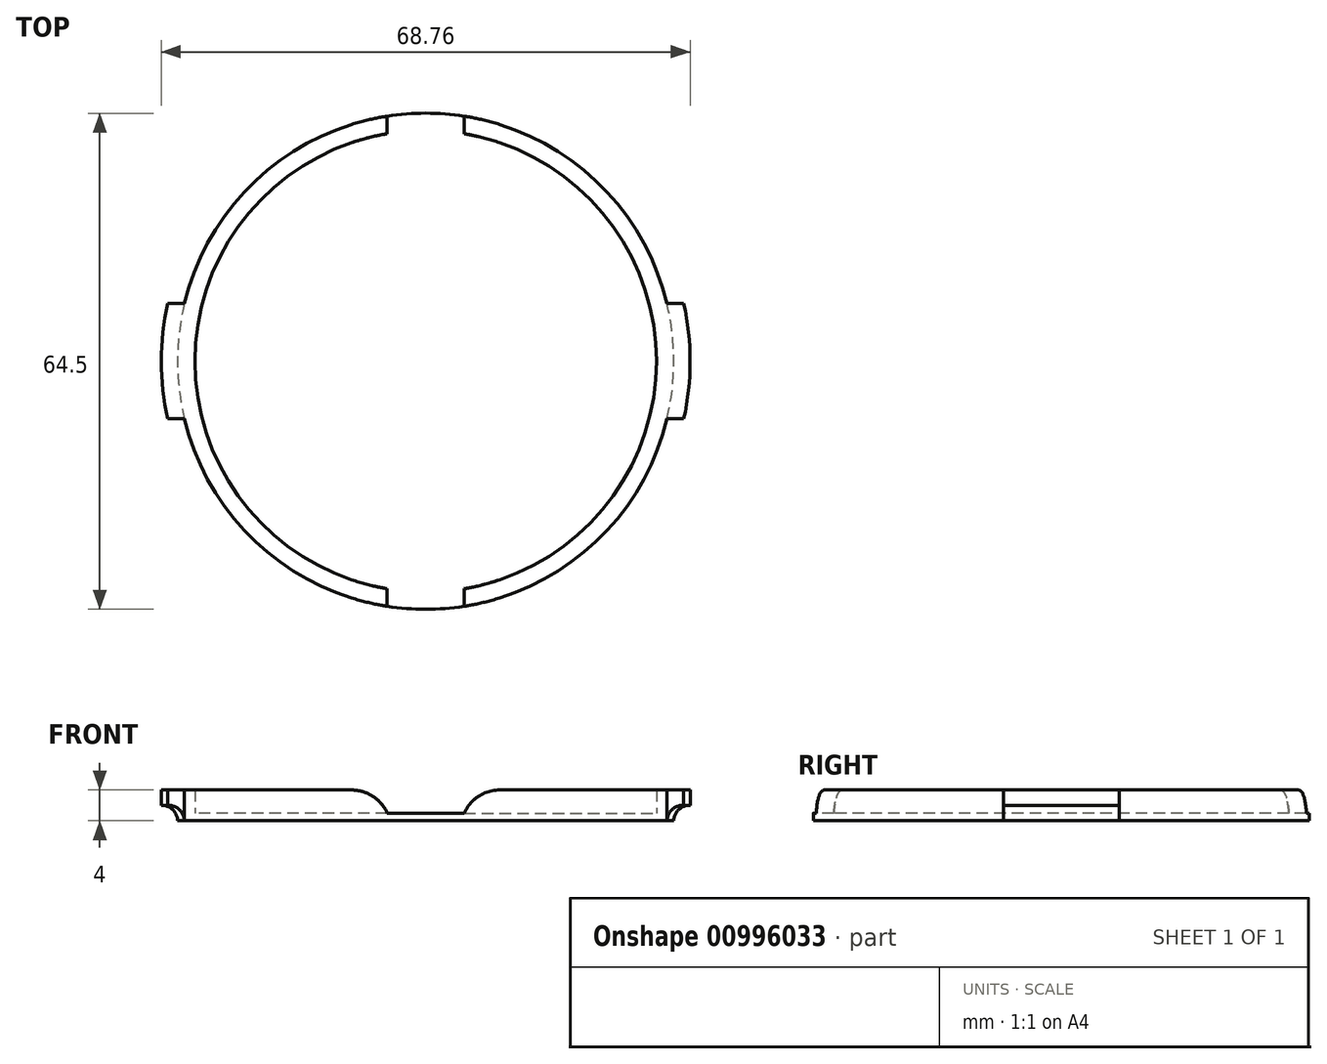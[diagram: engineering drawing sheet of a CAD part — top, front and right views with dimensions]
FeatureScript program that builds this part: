
annotation { "Feature Type Name" : "Feature", "Feature Type Description" : "" }
export const myFeature = defineFeature(function(context is Context, id is Id, definition is map)
    precondition{}
    {
        {
            var Q0;
            Q0=qCreatedBy(makeId("Top.planeOp"),FACE);
            var sketch = newSketch(context, id + "F0", { "sketchPlane" : qUnion([Q0])});
            skCircle(sketch, "E0", {"center": v(0, 0) * mm, "radius": 32.25 * mm});
            skSolve(sketch);
        }
        {
            var Q0;
            Q0=qSketchRegion(id+"F0",true);
            extrude(context, id + "F1", {"entities" : qUnion([Q0]), "oppositeDirection" : true, "depth" : 1 * mm, "offsetDistance" : 25.4 * mm});
        }
        {
            var Q0;
            Q0=qCreatedBy(makeId("Top.planeOp"),FACE);
            var sketch = newSketch(context, id + "F2", { "sketchPlane" : qUnion([Q0])});
            skCircle(sketch, "E1", {"center": v(0, 0) * mm, "radius": 30 * mm});
            skCircle(sketch, "E2", {"center": v(0, 0) * mm, "radius": 32.25 * mm});
            skSolve(sketch);
        }
        {
            var Q0;
            Q0=qSketchRegion(id+"F2",true);
            extrude(context, id + "F3", {"entities" : qUnion([Q0]), "operationType" : NewBodyOperationType.ADD, "depth" : 3 * mm, "offsetDistance" : 25.4 * mm});
        }
        {
            var Q0;
            Q0=makeQuery(id+"F3.opExtrude","CAP_FACE",FACE,{"disambiguationData":[OSD([sQuery(id+"F2.wireOp",EDGE,"E1"),sQuery(id+"F2.wireOp",EDGE,"E2")])],"isStart":false});
            var sketch = newSketch(context, id + "F4", { "sketchPlane" : qUnion([Q0])});
            skArc(sketch, "E3", {"start": v(-30, 0) * mm, "mid": v(-29.76, -3.78) * mm, "end": v(-29.05, -7.5) * mm});
            skLineSegment(sketch, "E4", {"start": v(-30, 0) * mm, "end": v(0, 0) * mm, "construction": true});
            skArc(sketch, "E5.MirrorCS", {"start": v(-30, 0) * mm, "mid": v(-29.76, 3.78) * mm, "end": v(-29.05, 7.5) * mm});
            skArc(sketch, "E6", {"start": v(-33.55, 7.5) * mm, "mid": v(-34.38, 0) * mm, "end": v(-33.55, -7.5) * mm});
            skLineSegment(sketch, "E7", {"start": v(-33.55, 7.5) * mm, "end": v(-29.05, 7.5) * mm});
            skLineSegment(sketch, "E8", {"start": v(-33.55, -7.5) * mm, "end": v(-29.05, -7.5) * mm});
            skLineSegment(sketch, "E9", {"start": v(0, 0) * mm, "end": v(0, 30) * mm, "construction": true});
            skLineSegment(sketch, "E10.MirrorCS", {"start": v(33.55, -7.5) * mm, "end": v(29.05, -7.5) * mm});
            skArc(sketch, "E11.MirrorCS", {"start": v(30, 0) * mm, "mid": v(29.76, -3.78) * mm, "end": v(29.05, -7.5) * mm});
            skArc(sketch, "E12.MirrorCS", {"start": v(30, 0) * mm, "mid": v(29.76, 3.78) * mm, "end": v(29.05, 7.5) * mm});
            skArc(sketch, "E13.MirrorCS", {"start": v(33.55, 7.5) * mm, "mid": v(34.38, 0) * mm, "end": v(33.55, -7.5) * mm});
            skLineSegment(sketch, "E14.MirrorCS", {"start": v(33.55, 7.5) * mm, "end": v(29.05, 7.5) * mm});
            skLineSegment(sketch, "E15", {"start": v(-34.38, 0) * mm, "end": v(34.38, 0) * mm});
            skSolve(sketch);
        }
        {
            var Q0;
            Q0=qSketchRegion(id+"F4",true);
            extrude(context, id + "F5", {"entities" : qUnion([Q0]), "operationType" : NewBodyOperationType.ADD, "oppositeDirection" : true, "depth" : 2 * mm, "offsetDistance" : 25.4 * mm});
        }
        {
            var Q0;
            Q0=qCreatedBy(makeId("Top.planeOp"),FACE);
            var sketch = newSketch(context, id + "F6", { "sketchPlane" : qUnion([Q0])});
            skLineSegment(sketch, "E16.bottom", {"start": v(5, 38.1) * mm, "end": v(-5, 38.1) * mm});
            skLineSegment(sketch, "E16.top", {"start": v(5, -38.1) * mm, "end": v(-5, -38.1) * mm});
            skLineSegment(sketch, "E16.left", {"start": v(5, 38.1) * mm, "end": v(5, -38.1) * mm});
            skLineSegment(sketch, "E16.right", {"start": v(-5, 38.1) * mm, "end": v(-5, -38.1) * mm});
            skPoint(sketch, "E16.middle", {"position": v(0, 0) * mm});
            skSolve(sketch);
        }
        {
            var Q0;
            Q0=qSketchRegion(id+"F6",true);
            extrude(context, id + "F7", {"entities" : qUnion([Q0]), "operationType" : NewBodyOperationType.REMOVE, "depth" : 25.4 * mm, "offsetDistance" : 25.4 * mm});
        }
        {
            var Q0;
            Q0=makeQuery(id+"F7.boolean.opBoolean","INTERSECT",EDGE,{"disambiguationData":[OD(0.0)],"derivedFrom":[makeQuery(id+"F5.boolean.opBoolean","MERGE",FACE,{"derivedFrom":[makeQuery(id+"F3.opExtrude","CAP_FACE",FACE,{"disambiguationData":[OSD([sQuery(id+"F2.wireOp",EDGE,"E1"),sQuery(id+"F2.wireOp",EDGE,"E2")])],"isStart":false}),makeQuery(id+"F5.opExtrude","CAP_FACE",FACE,{"disambiguationData":[OSD([sQuery(id+"F4.wireOp",EDGE,"E3"),sQuery(id+"F4.wireOp",EDGE,"E5.MirrorCS"),sQuery(id+"F4.wireOp",EDGE,"E6"),sQuery(id+"F4.wireOp",EDGE,"E7"),sQuery(id+"F4.wireOp",EDGE,"E8")])],"isStart":true}),makeQuery(id+"F5.opExtrude","CAP_FACE",FACE,{"disambiguationData":[OSD([sQuery(id+"F4.wireOp",EDGE,"E10.MirrorCS"),sQuery(id+"F4.wireOp",EDGE,"E11.MirrorCS"),sQuery(id+"F4.wireOp",EDGE,"E12.MirrorCS"),sQuery(id+"F4.wireOp",EDGE,"E13.MirrorCS"),sQuery(id+"F4.wireOp",EDGE,"E14.MirrorCS")])],"isStart":true})]}),makeQuery(id+"F7.opExtrude","SWEPT_FACE",FACE,{"disambiguationData":[OSD([sQuery(id+"F6.wireOp",EDGE,"E16.right")])]})]});
            var Q1;
            Q1=makeQuery(id+"F7.boolean.opBoolean","INTERSECT",EDGE,{"disambiguationData":[OD(0.0)],"derivedFrom":[makeQuery(id+"F5.boolean.opBoolean","MERGE",FACE,{"derivedFrom":[makeQuery(id+"F3.opExtrude","CAP_FACE",FACE,{"disambiguationData":[OSD([sQuery(id+"F2.wireOp",EDGE,"E1"),sQuery(id+"F2.wireOp",EDGE,"E2")])],"isStart":false}),makeQuery(id+"F5.opExtrude","CAP_FACE",FACE,{"disambiguationData":[OSD([sQuery(id+"F4.wireOp",EDGE,"E3"),sQuery(id+"F4.wireOp",EDGE,"E5.MirrorCS"),sQuery(id+"F4.wireOp",EDGE,"E6"),sQuery(id+"F4.wireOp",EDGE,"E7"),sQuery(id+"F4.wireOp",EDGE,"E8")])],"isStart":true}),makeQuery(id+"F5.opExtrude","CAP_FACE",FACE,{"disambiguationData":[OSD([sQuery(id+"F4.wireOp",EDGE,"E10.MirrorCS"),sQuery(id+"F4.wireOp",EDGE,"E11.MirrorCS"),sQuery(id+"F4.wireOp",EDGE,"E12.MirrorCS"),sQuery(id+"F4.wireOp",EDGE,"E13.MirrorCS"),sQuery(id+"F4.wireOp",EDGE,"E14.MirrorCS")])],"isStart":true})]}),makeQuery(id+"F7.opExtrude","SWEPT_FACE",FACE,{"disambiguationData":[OSD([sQuery(id+"F6.wireOp",EDGE,"E16.left")])]})]});
            var Q2;
            Q2=makeQuery(id+"F7.boolean.opBoolean","INTERSECT",EDGE,{"disambiguationData":[OD(1.0)],"derivedFrom":[makeQuery(id+"F5.boolean.opBoolean","MERGE",FACE,{"derivedFrom":[makeQuery(id+"F3.opExtrude","CAP_FACE",FACE,{"disambiguationData":[OSD([sQuery(id+"F2.wireOp",EDGE,"E1"),sQuery(id+"F2.wireOp",EDGE,"E2")])],"isStart":false}),makeQuery(id+"F5.opExtrude","CAP_FACE",FACE,{"disambiguationData":[OSD([sQuery(id+"F4.wireOp",EDGE,"E3"),sQuery(id+"F4.wireOp",EDGE,"E5.MirrorCS"),sQuery(id+"F4.wireOp",EDGE,"E6"),sQuery(id+"F4.wireOp",EDGE,"E7"),sQuery(id+"F4.wireOp",EDGE,"E8")])],"isStart":true}),makeQuery(id+"F5.opExtrude","CAP_FACE",FACE,{"disambiguationData":[OSD([sQuery(id+"F4.wireOp",EDGE,"E10.MirrorCS"),sQuery(id+"F4.wireOp",EDGE,"E11.MirrorCS"),sQuery(id+"F4.wireOp",EDGE,"E12.MirrorCS"),sQuery(id+"F4.wireOp",EDGE,"E13.MirrorCS"),sQuery(id+"F4.wireOp",EDGE,"E14.MirrorCS")])],"isStart":true})]}),makeQuery(id+"F7.opExtrude","SWEPT_FACE",FACE,{"disambiguationData":[OSD([sQuery(id+"F6.wireOp",EDGE,"E16.right")])]})]});
            var Q3;
            Q3=makeQuery(id+"F7.boolean.opBoolean","INTERSECT",EDGE,{"disambiguationData":[OD(1.0)],"derivedFrom":[makeQuery(id+"F5.boolean.opBoolean","MERGE",FACE,{"derivedFrom":[makeQuery(id+"F3.opExtrude","CAP_FACE",FACE,{"disambiguationData":[OSD([sQuery(id+"F2.wireOp",EDGE,"E1"),sQuery(id+"F2.wireOp",EDGE,"E2")])],"isStart":false}),makeQuery(id+"F5.opExtrude","CAP_FACE",FACE,{"disambiguationData":[OSD([sQuery(id+"F4.wireOp",EDGE,"E3"),sQuery(id+"F4.wireOp",EDGE,"E5.MirrorCS"),sQuery(id+"F4.wireOp",EDGE,"E6"),sQuery(id+"F4.wireOp",EDGE,"E7"),sQuery(id+"F4.wireOp",EDGE,"E8")])],"isStart":true}),makeQuery(id+"F5.opExtrude","CAP_FACE",FACE,{"disambiguationData":[OSD([sQuery(id+"F4.wireOp",EDGE,"E10.MirrorCS"),sQuery(id+"F4.wireOp",EDGE,"E11.MirrorCS"),sQuery(id+"F4.wireOp",EDGE,"E12.MirrorCS"),sQuery(id+"F4.wireOp",EDGE,"E13.MirrorCS"),sQuery(id+"F4.wireOp",EDGE,"E14.MirrorCS")])],"isStart":true})]}),makeQuery(id+"F7.opExtrude","SWEPT_FACE",FACE,{"disambiguationData":[OSD([sQuery(id+"F6.wireOp",EDGE,"E16.left")])]})]});
            fillet(context, id + "F8", {"entities" : qUnion([Q0, Q1, Q2, Q3]), "radius" : 5.08 * mm, "tangentPropagation" : true, "allowEdgeOverflow" : false});
        }
        {
            var Q0;
            Q0=makeQuery(id+"F5.boolean.opBoolean","INTERSECT",EDGE,{"derivedFrom":[makeQuery(id+"F3.boolean.opBoolean","MERGE",FACE,{"derivedFrom":[makeQuery(id+"F1.opExtrude","SWEPT_FACE",FACE,{"disambiguationData":[OSD([sQuery(id+"F0.wireOp",EDGE,"E0")])]}),makeQuery(id+"F3.opExtrude","SWEPT_FACE",FACE,{"disambiguationData":[OSD([sQuery(id+"F2.wireOp",EDGE,"E2")])]})]}),makeQuery(id+"F5.opExtrude","CAP_FACE",FACE,{"disambiguationData":[OSD([sQuery(id+"F4.wireOp",EDGE,"E3"),sQuery(id+"F4.wireOp",EDGE,"E5.MirrorCS"),sQuery(id+"F4.wireOp",EDGE,"E6"),sQuery(id+"F4.wireOp",EDGE,"E7"),sQuery(id+"F4.wireOp",EDGE,"E8")])],"isStart":false})]});
            var Q1;
            Q1=makeQuery(id+"F5.boolean.opBoolean","INTERSECT",EDGE,{"derivedFrom":[makeQuery(id+"F3.boolean.opBoolean","MERGE",FACE,{"derivedFrom":[makeQuery(id+"F1.opExtrude","SWEPT_FACE",FACE,{"disambiguationData":[OSD([sQuery(id+"F0.wireOp",EDGE,"E0")])]}),makeQuery(id+"F3.opExtrude","SWEPT_FACE",FACE,{"disambiguationData":[OSD([sQuery(id+"F2.wireOp",EDGE,"E2")])]})]}),makeQuery(id+"F5.opExtrude","CAP_FACE",FACE,{"disambiguationData":[OSD([sQuery(id+"F4.wireOp",EDGE,"E10.MirrorCS"),sQuery(id+"F4.wireOp",EDGE,"E11.MirrorCS"),sQuery(id+"F4.wireOp",EDGE,"E12.MirrorCS"),sQuery(id+"F4.wireOp",EDGE,"E13.MirrorCS"),sQuery(id+"F4.wireOp",EDGE,"E14.MirrorCS")])],"isStart":false})]});
            fillet(context, id + "F9", {"entities" : qUnion([Q0, Q1]), "radius" : 2.03 * mm, "tangentPropagation" : true, "allowEdgeOverflow" : false});
        }
    });
